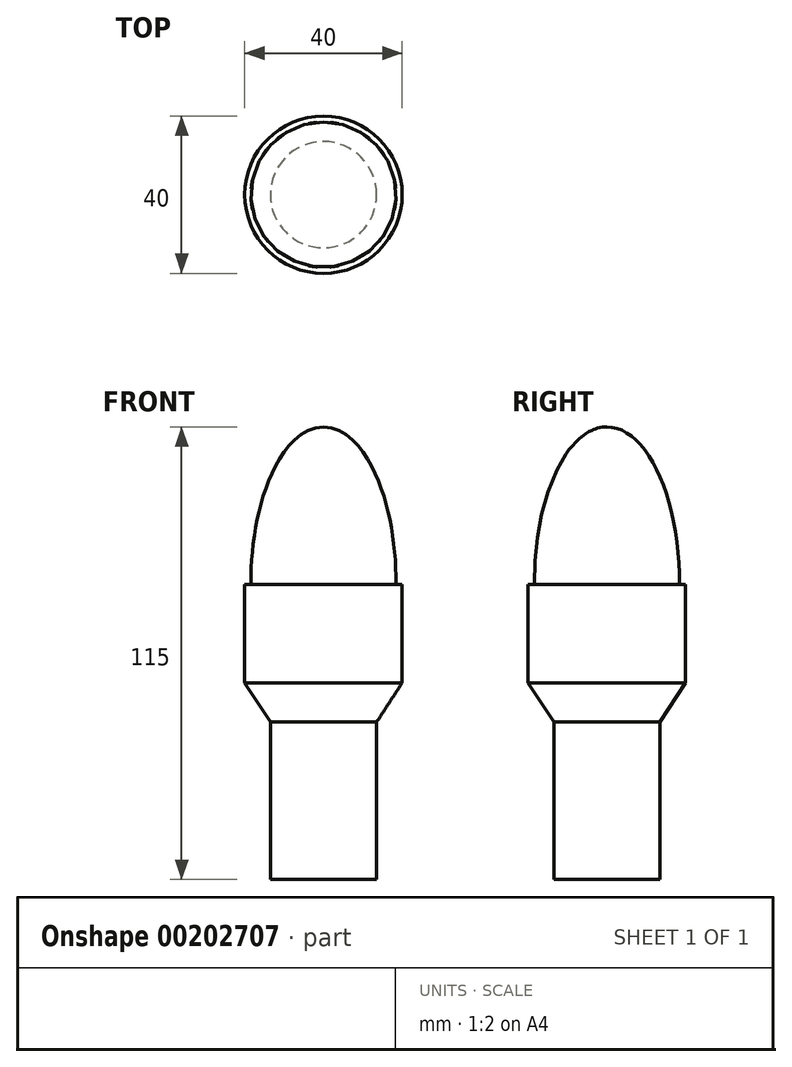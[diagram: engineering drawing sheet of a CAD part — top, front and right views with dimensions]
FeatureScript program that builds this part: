
annotation { "Feature Type Name" : "Feature", "Feature Type Description" : "" }
export const myFeature = defineFeature(function(context is Context, id is Id, definition is map)
    precondition{}
    {
        {
            var Q0;
            Q0=qCreatedBy(makeId("Top.planeOp"),FACE);
            var sketch = newSketch(context, id + "F0", { "sketchPlane" : qUnion([Q0])});
            skCircle(sketch, "E0", {"center": v(0, 0) * mm, "radius": 13.5 * mm});
            skSolve(sketch);
        }
        {
            var Q0;
            Q0=makeQuery(id+"F0.imprint","IMPRINT",FACE,{"disambiguationData":[TD([[makeQuery(id+"F0.imprint","IMPRINT",EDGE,{"derivedFrom":sQuery(id+"F0.wireOp",EDGE,"E0")}),1.0]])]});
            extrude(context, id + "F1", {"entities" : qUnion([Q0]), "depth" : 40 * mm});
        }
        {
            var Q0;
            Q0=makeQuery(id+"F1.opExtrude","CAP_FACE",FACE,{"disambiguationData":[OSD([sQuery(id+"F0.wireOp",EDGE,"E0")])],"isStart":false});
            extrude(context, id + "F2", {"entities" : qUnion([Q0]), "operationType" : NewBodyOperationType.ADD, "depth" : 10 * mm, "hasDraft" : true, "draftAngle" : 33.02 * degree});
        }
        {
            var Q0;
            Q0=makeQuery(id+"F2.opExtrude","CAP_FACE",FACE,{"disambiguationData":[OSD([sQuery(id+"F0.wireOp",EDGE,"E0")])],"isStart":false});
            extrude(context, id + "F3", {"entities" : qUnion([Q0]), "operationType" : NewBodyOperationType.ADD, "depth" : 25 * mm});
        }
        {
            var Q0;
            Q0=qCreatedBy(makeId("Right.planeOp"),FACE);
            var sketch = newSketch(context, id + "F4", { "sketchPlane" : qUnion([Q0])});
            skLineSegment(sketch, "E1", {"start": v(0, 0) * mm, "end": v(0, 115) * mm});
            skEllipse(sketch, "E2", {"center": v(0, 75.33) * mm, "majorRadius": 39.67 * mm, "minorRadius": 18.44 * mm, "majorAxis": v(0, 1)});
            skSolve(sketch);
        }
        {
            var Q0;
            {var subQ0=sQuery(id+"F4.wireOp",EDGE,"E2");var subQ1=sQuery(id+"F4.wireOp",EDGE,"E1");var subQ2=makeQuery(id+"F4.imprint","INTERSECT",VERTEX,{"disambiguationData":[OD(0.0)],"derivedFrom":[subQ1,subQ0]});Q0=makeQuery(id+"F4.imprint","IMPRINT",FACE,{"disambiguationData":[TD([[makeQuery(id+"F4.imprint","IMPRINT",EDGE,{"disambiguationData":[TD([[subQ2,1.0]])],"derivedFrom":subQ1}),-1.0]])]});}
            var Q1;
            Q1=sQuery(id+"F4.wireOp",EDGE,"E1");
            revolve(context, id + "F5", {"operationType" : NewBodyOperationType.ADD, "entities" : qUnion([Q0]), "axis" : qUnion([Q1]), "revolveType" : RevolveType.FULL});
        }
    });
